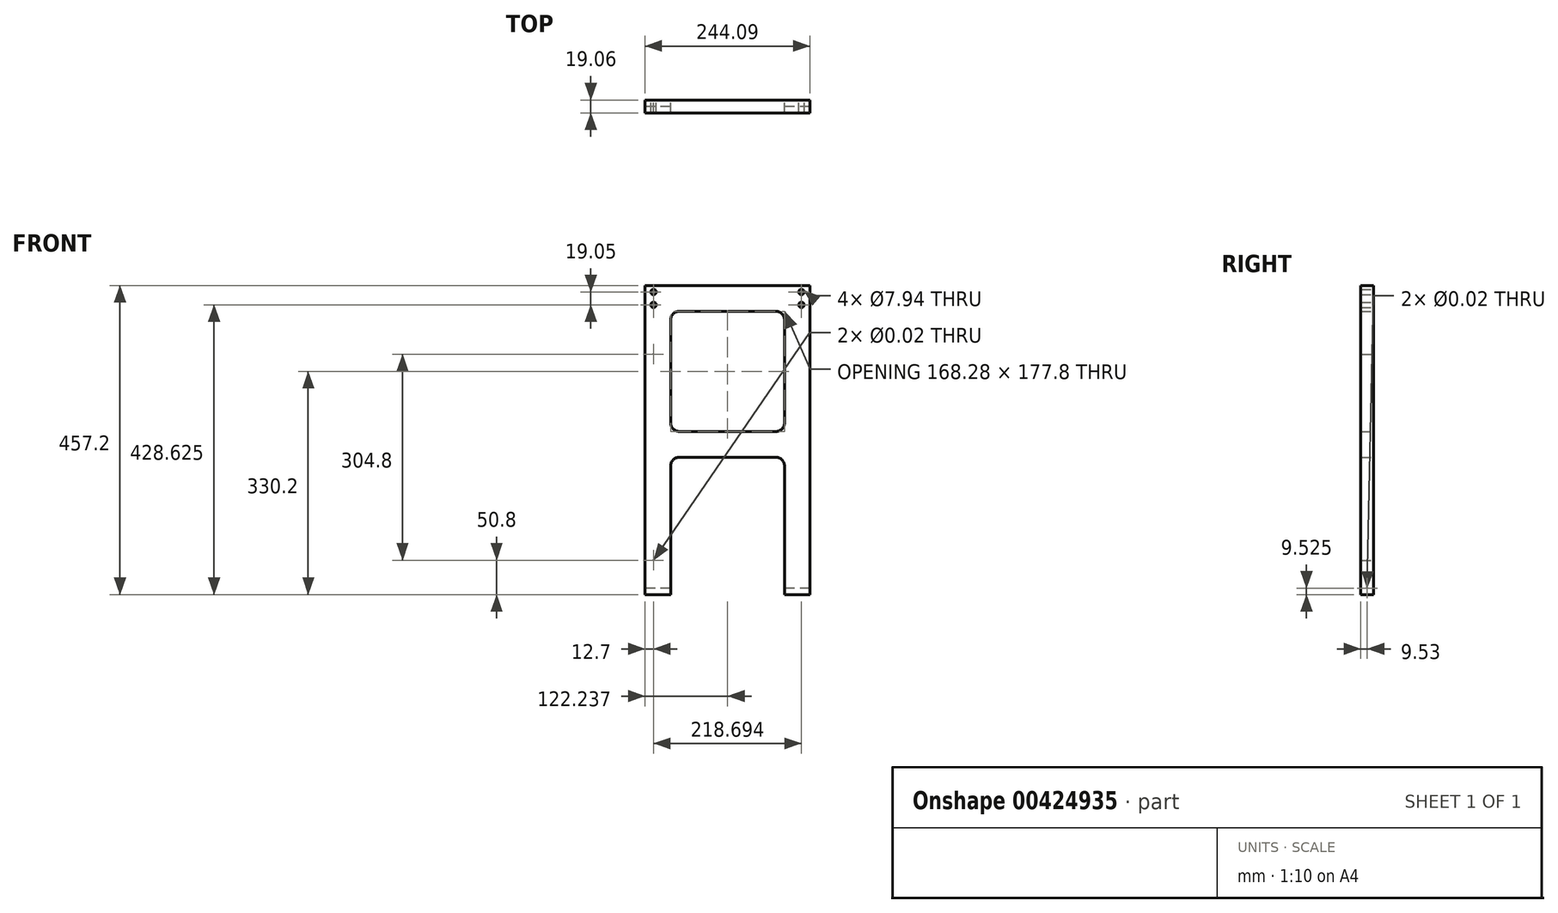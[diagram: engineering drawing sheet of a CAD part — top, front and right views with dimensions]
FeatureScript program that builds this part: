
annotation { "Feature Type Name" : "Feature", "Feature Type Description" : "" }
export const myFeature = defineFeature(function(context is Context, id is Id, definition is map)
    precondition{}
    {
        {
            var Q0;
            Q0=qCreatedBy(makeId("Front.planeOp"),FACE);
            var sketch = newSketch(context, id + "F0", { "sketchPlane" : qUnion([Q0])});
            skLineSegment(sketch, "E0", {"start": v(0, 0) * mm, "end": v(244.1, 0) * mm});
            skLineSegment(sketch, "E1", {"start": v(244.1, 0) * mm, "end": v(244.1, -457.2) * mm});
            skLineSegment(sketch, "E2", {"start": v(244.1, -457.2) * mm, "end": v(206.38, -457.2) * mm});
            skLineSegment(sketch, "E3", {"start": v(206.38, -457.2) * mm, "end": v(206.38, -254) * mm});
            skLineSegment(sketch, "E4", {"start": v(206.38, -254) * mm, "end": v(38.1, -254) * mm});
            skLineSegment(sketch, "E5", {"start": v(38.1, -254) * mm, "end": v(38.1, -457.2) * mm});
            skLineSegment(sketch, "E6", {"start": v(38.1, -457.2) * mm, "end": v(0, -457.2) * mm});
            skLineSegment(sketch, "E7", {"start": v(0, -457.2) * mm, "end": v(0, 0) * mm});
            skLineSegment(sketch, "E8", {"start": v(38.1, -38.1) * mm, "end": v(38.1, -215.9) * mm});
            skLineSegment(sketch, "E9", {"start": v(38.1, -215.9) * mm, "end": v(206.38, -215.9) * mm});
            skLineSegment(sketch, "E10", {"start": v(206.38, -215.9) * mm, "end": v(206.38, -38.1) * mm});
            skLineSegment(sketch, "E11", {"start": v(206.38, -38.1) * mm, "end": v(38.1, -38.1) * mm});
            skSolve(sketch);
        }
        {
            var Q0;
            Q0 = qSketchRegion(id + "F0", true);
            extrude(context, id + "F1", {"entities" : qUnion([Q0]), "depth" : 19.05 * mm, "symmetric" : true});
        }
        {
            var Q0;
            Q0=makeQuery(id+"F1.opExtrude","SWEPT_FACE",FACE,{"disambiguationData":[OSD([sQuery(id+"F0.wireOp",EDGE,"E1")])]});
            var sketch = newSketch(context, id + "F2", { "sketchPlane" : qUnion([Q0])});
            skPoint(sketch, "E12", {"position": v(0, -447.68) * mm});
            skPoint(sketch, "E12.positionSnap0", {"position": v(0, -457.2) * mm});
            skSolve(sketch);
        }
        {
            var Q0;
            Q0=sQuery(id+"F2.wireOp",VERTEX,"E12");
            var Q1;
            Q1=makeQuery(id+"F1.opExtrude","SWEPT_BODY",BODY,{"disambiguationData":[OSD([sQuery(id+"F0.wireOp",EDGE,"E0"),sQuery(id+"F0.wireOp",EDGE,"E1"),sQuery(id+"F0.wireOp",EDGE,"E2"),sQuery(id+"F0.wireOp",EDGE,"E3"),sQuery(id+"F0.wireOp",EDGE,"E4"),sQuery(id+"F0.wireOp",EDGE,"E5"),sQuery(id+"F0.wireOp",EDGE,"E6"),sQuery(id+"F0.wireOp",EDGE,"E7"),sQuery(id+"F0.wireOp",EDGE,"E8"),sQuery(id+"F0.wireOp",EDGE,"E9"),sQuery(id+"F0.wireOp",EDGE,"E10"),sQuery(id+"F0.wireOp",EDGE,"E11")])]});
            hole(context, id + "F3", {"style" : HoleStyle.SIMPLE, "endStyle" : HoleEndStyle.THROUGH, "standardTappedOrClearance" : lookupTablePath({ "standard" : "ANSI", "size" : "1/2 (0.5)", "type" : "Drilled" }), "standardBlindInLast" : lookupTablePath({ "standard" : "ANSI", "size" : "1/2", "type" : "Drilled" }), "holeDiameter" : 1 / 50.8 * mm, "isTappedThrough" : true, "tappedDepth" : 22.25 * mm, "tapClearance" : 3, "locations" : qUnion([Q0]), "scope" : qUnion([Q1]), "startStyle" : HoleStartStyle.SKETCH});
        }
        {
            var Q0;
            Q0=makeQuery(id+"F1.opExtrude","CAP_FACE",FACE,{"disambiguationData":[OSD([sQuery(id+"F0.wireOp",EDGE,"E0"),sQuery(id+"F0.wireOp",EDGE,"E1"),sQuery(id+"F0.wireOp",EDGE,"E2"),sQuery(id+"F0.wireOp",EDGE,"E3"),sQuery(id+"F0.wireOp",EDGE,"E4"),sQuery(id+"F0.wireOp",EDGE,"E5"),sQuery(id+"F0.wireOp",EDGE,"E6"),sQuery(id+"F0.wireOp",EDGE,"E7"),sQuery(id+"F0.wireOp",EDGE,"E8"),sQuery(id+"F0.wireOp",EDGE,"E9"),sQuery(id+"F0.wireOp",EDGE,"E10"),sQuery(id+"F0.wireOp",EDGE,"E11")])],"isStart":false});
            var sketch = newSketch(context, id + "F4", { "sketchPlane" : qUnion([Q0])});
            skLineSegment(sketch, "E13", {"start": v(12.7, -101.6) * mm, "end": v(12.7, -406.4) * mm, "construction": true});
            skPoint(sketch, "E14", {"position": v(12.7, -101.6) * mm});
            skPoint(sketch, "E15", {"position": v(12.7, -406.4) * mm});
            skSolve(sketch);
        }
        {
            var Q0;
            Q0=sQuery(id+"F4.wireOp",VERTEX,"E15");
            var Q1;
            Q1=sQuery(id+"F4.wireOp",VERTEX,"E14");
            var Q2;
            Q2=makeQuery(id+"F1.opExtrude","SWEPT_BODY",BODY,{"disambiguationData":[OSD([sQuery(id+"F0.wireOp",EDGE,"E0"),sQuery(id+"F0.wireOp",EDGE,"E1"),sQuery(id+"F0.wireOp",EDGE,"E2"),sQuery(id+"F0.wireOp",EDGE,"E3"),sQuery(id+"F0.wireOp",EDGE,"E4"),sQuery(id+"F0.wireOp",EDGE,"E5"),sQuery(id+"F0.wireOp",EDGE,"E6"),sQuery(id+"F0.wireOp",EDGE,"E7"),sQuery(id+"F0.wireOp",EDGE,"E8"),sQuery(id+"F0.wireOp",EDGE,"E9"),sQuery(id+"F0.wireOp",EDGE,"E10"),sQuery(id+"F0.wireOp",EDGE,"E11")])]});
            hole(context, id + "F5", {"style" : HoleStyle.SIMPLE, "endStyle" : HoleEndStyle.THROUGH, "standardTappedOrClearance" : lookupTablePath({ "standard" : "ANSI", "size" : "1/2 (0.5)", "type" : "Drilled" }), "standardBlindInLast" : lookupTablePath({ "standard" : "ANSI", "size" : "1/2", "type" : "Drilled" }), "holeDiameter" : 1 / 50.8 * mm, "isTappedThrough" : true, "tappedDepth" : 22.25 * mm, "tapClearance" : 3, "locations" : qUnion([Q0, Q1]), "scope" : qUnion([Q2]), "startStyle" : HoleStartStyle.SKETCH});
        }
        {
            var Q0;
            Q0=makeQuery(id+"F1.opExtrude","CAP_FACE",FACE,{"disambiguationData":[OSD([sQuery(id+"F0.wireOp",EDGE,"E0"),sQuery(id+"F0.wireOp",EDGE,"E1"),sQuery(id+"F0.wireOp",EDGE,"E2"),sQuery(id+"F0.wireOp",EDGE,"E3"),sQuery(id+"F0.wireOp",EDGE,"E4"),sQuery(id+"F0.wireOp",EDGE,"E5"),sQuery(id+"F0.wireOp",EDGE,"E6"),sQuery(id+"F0.wireOp",EDGE,"E7"),sQuery(id+"F0.wireOp",EDGE,"E8"),sQuery(id+"F0.wireOp",EDGE,"E9"),sQuery(id+"F0.wireOp",EDGE,"E10"),sQuery(id+"F0.wireOp",EDGE,"E11")])],"isStart":false});
            var sketch = newSketch(context, id + "F6", { "sketchPlane" : qUnion([Q0])});
            skLineSegment(sketch, "E16.bottom", {"start": v(12.7, -9.53) * mm, "end": v(231.4, -9.52) * mm, "construction": true});
            skLineSegment(sketch, "E16.top", {"start": v(12.7, -28.58) * mm, "end": v(231.4, -28.57) * mm, "construction": true});
            skLineSegment(sketch, "E16.left", {"start": v(12.7, -9.53) * mm, "end": v(12.7, -28.58) * mm, "construction": true});
            skLineSegment(sketch, "E16.right", {"start": v(231.4, -9.52) * mm, "end": v(231.4, -28.57) * mm, "construction": true});
            skPoint(sketch, "E17", {"position": v(231.4, -28.57) * mm});
            skPoint(sketch, "E18", {"position": v(231.4, -9.52) * mm});
            skPoint(sketch, "E19", {"position": v(12.7, -9.53) * mm});
            skPoint(sketch, "E20", {"position": v(12.7, -28.58) * mm});
            skSolve(sketch);
        }
        {
            var Q0;
            Q0=sQuery(id+"F6.wireOp",VERTEX,"E19");
            var Q1;
            Q1=sQuery(id+"F6.wireOp",VERTEX,"E20");
            var Q2;
            Q2=sQuery(id+"F6.wireOp",VERTEX,"E17");
            var Q3;
            Q3=sQuery(id+"F6.wireOp",VERTEX,"E18");
            var Q4;
            Q4=makeQuery(id+"F1.opExtrude","SWEPT_BODY",BODY,{"disambiguationData":[OSD([sQuery(id+"F0.wireOp",EDGE,"E0"),sQuery(id+"F0.wireOp",EDGE,"E1"),sQuery(id+"F0.wireOp",EDGE,"E2"),sQuery(id+"F0.wireOp",EDGE,"E3"),sQuery(id+"F0.wireOp",EDGE,"E4"),sQuery(id+"F0.wireOp",EDGE,"E5"),sQuery(id+"F0.wireOp",EDGE,"E6"),sQuery(id+"F0.wireOp",EDGE,"E7"),sQuery(id+"F0.wireOp",EDGE,"E8"),sQuery(id+"F0.wireOp",EDGE,"E9"),sQuery(id+"F0.wireOp",EDGE,"E10"),sQuery(id+"F0.wireOp",EDGE,"E11")])]});
            hole(context, id + "F7", {"style" : HoleStyle.SIMPLE, "endStyle" : HoleEndStyle.THROUGH, "standardTappedOrClearance" : lookupTablePath({ "standard" : "ANSI", "engagement" : "75%", "pitch" : "16 tpi", "size" : "3/8", "type" : "Tapped" }), "standardBlindInLast" : lookupTablePath({ "standard" : "ANSI", "engagement" : "75%", "pitch" : "16 tpi", "size" : "3/8", "type" : "Tapped" }), "holeDiameter" : 7.94 * mm, "showTappedDepth" : true, "isTappedThrough" : true, "tappedDepth" : 22.25 * mm, "tapClearance" : 3, "locations" : qUnion([Q0, Q1, Q2, Q3]), "scope" : qUnion([Q4]), "majorDiameter" : 9.53 * mm, "startStyle" : HoleStartStyle.SKETCH});
        }
        {
            var Q0;
            Q0=makeQuery(id+"F1.opExtrude","SWEPT_EDGE",EDGE,{"disambiguationData":[OSD([sQuery(id+"F0.wireOp",EDGE,"E8"),sQuery(id+"F0.wireOp",EDGE,"E11")])]});
            var Q1;
            Q1=makeQuery(id+"F1.opExtrude","SWEPT_EDGE",EDGE,{"disambiguationData":[OSD([sQuery(id+"F0.wireOp",EDGE,"E10"),sQuery(id+"F0.wireOp",EDGE,"E11")])]});
            var Q2;
            Q2=makeQuery(id+"F1.opExtrude","SWEPT_EDGE",EDGE,{"disambiguationData":[OSD([sQuery(id+"F0.wireOp",EDGE,"E9"),sQuery(id+"F0.wireOp",EDGE,"E10")])]});
            var Q3;
            Q3=makeQuery(id+"F1.opExtrude","SWEPT_EDGE",EDGE,{"disambiguationData":[OSD([sQuery(id+"F0.wireOp",EDGE,"E8"),sQuery(id+"F0.wireOp",EDGE,"E9")])]});
            var Q4;
            Q4=makeQuery(id+"F1.opExtrude","SWEPT_EDGE",EDGE,{"disambiguationData":[OSD([sQuery(id+"F0.wireOp",EDGE,"E3"),sQuery(id+"F0.wireOp",EDGE,"E4")])]});
            var Q5;
            Q5=makeQuery(id+"F1.opExtrude","SWEPT_EDGE",EDGE,{"disambiguationData":[OSD([sQuery(id+"F0.wireOp",EDGE,"E4"),sQuery(id+"F0.wireOp",EDGE,"E5")])]});
            fillet(context, id + "F8", {"entities" : qUnion([Q0, Q1, Q2, Q3, Q4, Q5]), "radius" : 12.7 * mm, "tangentPropagation" : true, "allowEdgeOverflow" : false});
        }
    });
